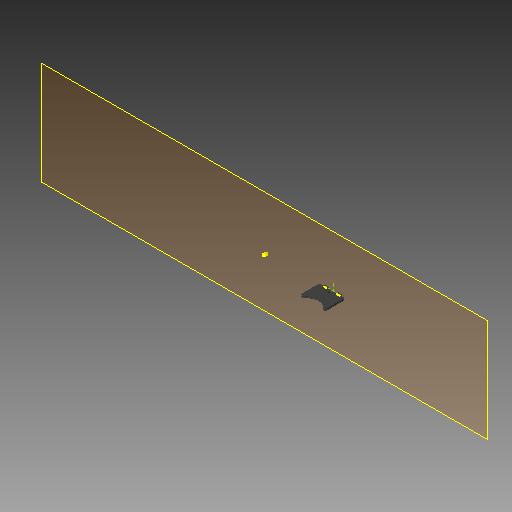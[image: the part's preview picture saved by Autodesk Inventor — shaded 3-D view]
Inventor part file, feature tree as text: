
AUTODESK INVENTOR PART (.ipt)
format: ipt  version: 2018 (Build 220112000, 112)  size: 184,320 bytes
history: native  units: mm
features: sketch x7, extrude x6, fillet x2, reference x2, projected_geometry x2, other x2, plane x1
ambient origin geometry x8: Origin, YZ Plane, XZ Plane, XY Plane, X Axis, Y Axis, Z Axis, Center Point
bodies: Solid1 (feature_tree)
feature tree (22):
  plane  "Work Plane1"
  extrude  "Extrusion1"  Depth=3.0mm
  sketch  "Sketch2"  dims[d2=6.0mm d3=3.0mm]
  extrude  "Extrusion2"  Depth=3.0mm
  extrude  "Extrusion3"  Depth=40.0mm
  fillet  "Fillet1"  Radius=3.0mm
  extrude  "Extrusion4"  Depth=40.0mm
  fillet  "Fillet2"  Radius=38.0mm
  extrude  "Extrusion5"  Depth=16.0mm
  sketch  "Sketch7"  dims[d17=2.0mm d18=40.0mm d19=0.0mm d20=2.0mm d21=1.5mm d22=10.7mm d23=1.5mm d24=6.0mm d25=1.2mm d26=2.0mm d27=40.0mm d28=0.0mm]
  sketch  "Sketch1"  dims[d0=6.0mm d1=3.0mm]
  reference  "Reference1"
  reference  "Reference2"
  projected_geometry  "Projected Loop1"
  projected_geometry  "Projected Loop2"
  sketch  "Sketch3"  dims[d4=3.0mm d5=0.0mm d6=40.0mm d7=3.0mm]
  sketch  "Sketch4"  dims[d8=60.0mm d9=0.0mm d10=40.0mm d11=38.0mm]
  sketch  "Sketch5"  dims[d12=16.0mm d13=16.0mm]
  sketch  "Sketch6"  dims[d14=3.2mm d15=40.0mm d16=0.0mm]
  other  "<userpath>\OneDrive\Inventor\Beast 3D Printer\Extruder Assembly.iam"
  extrude  "Extruder Assembly.iam"  Depth=40.0mm TaperAngle=0.0deg
  other  "Rear Extruder Panel:1"
